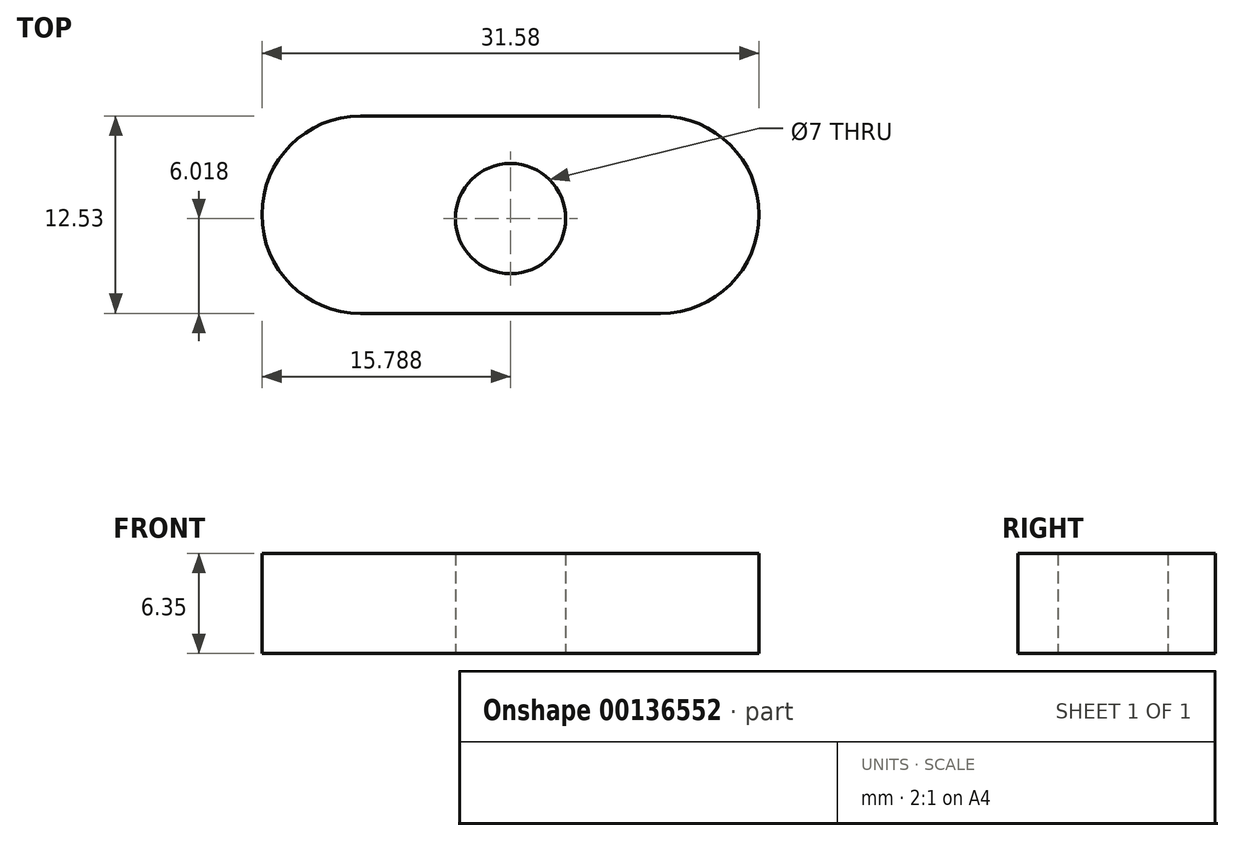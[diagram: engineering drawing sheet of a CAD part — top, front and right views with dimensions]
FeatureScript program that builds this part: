
annotation { "Feature Type Name" : "Feature", "Feature Type Description" : "" }
export const myFeature = defineFeature(function(context is Context, id is Id, definition is map)
    precondition{}
    {
        {
            var Q0;
            Q0=qCreatedBy(makeId("Top.planeOp"),FACE);
            var sketch = newSketch(context, id + "F0", { "sketchPlane" : qUnion([Q0])});
            skLineSegment(sketch, "E0", {"start": v(-28.15, 12.53) * mm, "end": v(-9.1, 12.53) * mm});
            skLineSegment(sketch, "E1", {"start": v(-28.15, 0) * mm, "end": v(-9.1, 0) * mm});
            skArc(sketch, "E2", {"start": v(-9.1, 0) * mm, "mid": v(-2.83, 6.27) * mm, "end": v(-9.1, 12.53) * mm});
            skArc(sketch, "E3", {"start": v(-28.15, 12.53) * mm, "mid": v(-34.41, 6.27) * mm, "end": v(-28.15, 0) * mm});
            skCircle(sketch, "E4", {"center": v(-18.62, 6.02) * mm, "radius": 3.5 * mm});
            skPoint(sketch, "E4.centerSnap0", {"position": v(-18.62, 12.53) * mm});
            skSolve(sketch);
        }
        {
            var Q0;
            Q0 = qSketchRegion(id + "F0", true);
            var Q1;
            Q1=makeQuery(id+"F0.imprint","IMPRINT",FACE,{"disambiguationData":[TD([[makeQuery(id+"F0.imprint","IMPRINT",EDGE,{"derivedFrom":sQuery(id+"F0.wireOp",EDGE,"E0")}),-1.0]])]});
            extrude(context, id + "F1", {"entities" : qUnion([Q0, Q1]), "depth" : 6.35 * mm});
        }
    });
